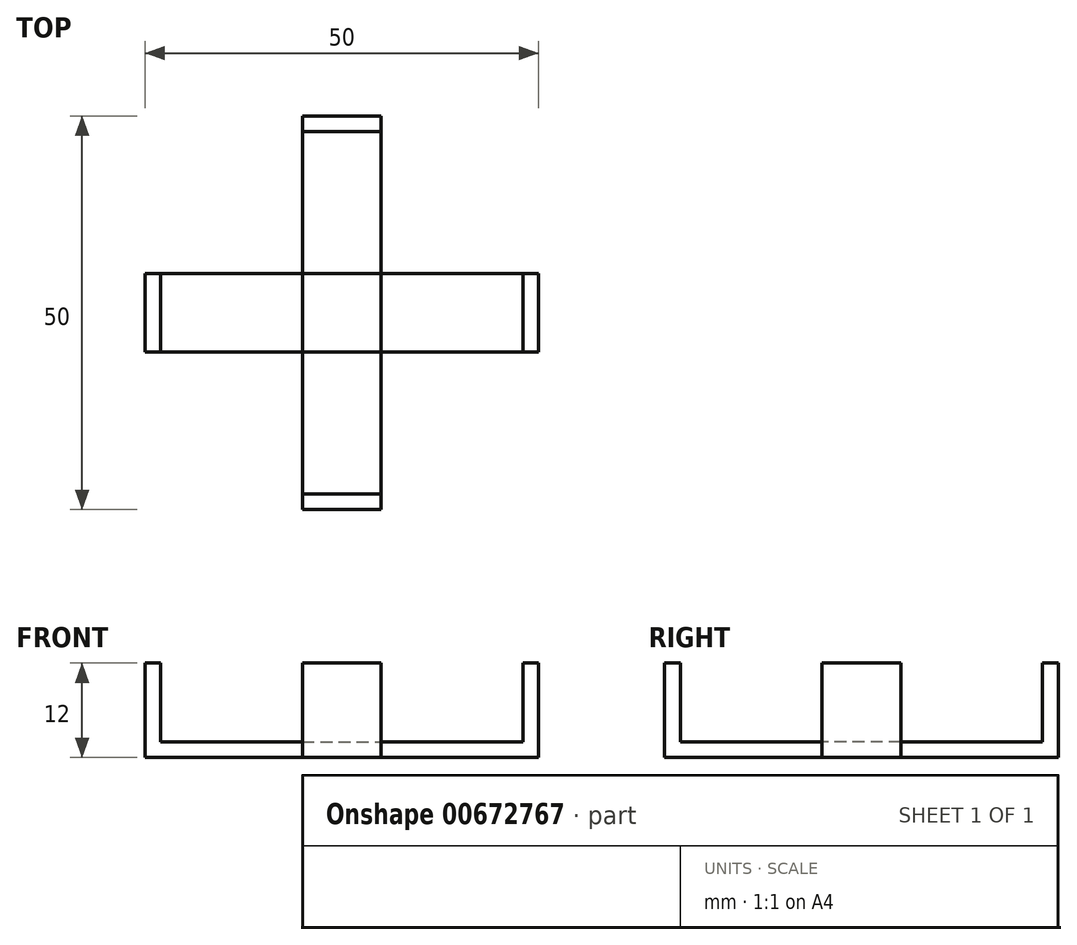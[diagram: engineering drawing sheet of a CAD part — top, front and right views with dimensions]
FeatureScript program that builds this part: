
annotation { "Feature Type Name" : "Feature", "Feature Type Description" : "" }
export const myFeature = defineFeature(function(context is Context, id is Id, definition is map)
    precondition{}
    {
        {
            var Q0;
            Q0=qCreatedBy(makeId("Top.planeOp"),FACE);
            var sketch = newSketch(context, id + "F0", { "sketchPlane" : qUnion([Q0])});
            skLineSegment(sketch, "E0.bottom", {"start": v(150, 80) * mm, "end": v(-150, 80) * mm});
            skLineSegment(sketch, "E0.top", {"start": v(150, -80) * mm, "end": v(-150, -80) * mm});
            skLineSegment(sketch, "E0.left", {"start": v(150, 80) * mm, "end": v(150, -80) * mm});
            skLineSegment(sketch, "E0.right", {"start": v(-150, 80) * mm, "end": v(-150, -80) * mm});
            skPoint(sketch, "E0.middle", {"position": v(0, 0) * mm});
            skSolve(sketch);
        }
        {
            var Q0;
            Q0=qSketchRegion(id+"F0",true);
            extrude(context, id + "F1", {"entities" : qUnion([Q0]), "depth" : 2 * mm, "offsetDistance" : 25 * mm});
        }
        {
            var Q0;
            Q0=makeQuery(id+"F1.opExtrude","CAP_FACE",FACE,{"disambiguationData":[OSD([sQuery(id+"F0.wireOp",EDGE,"E0.bottom"),sQuery(id+"F0.wireOp",EDGE,"E0.top"),sQuery(id+"F0.wireOp",EDGE,"E0.left"),sQuery(id+"F0.wireOp",EDGE,"E0.right")])],"isStart":false});
            var sketch = newSketch(context, id + "F2", { "sketchPlane" : qUnion([Q0])});
            skLineSegment(sketch, "E1.bottom", {"start": v(5, 5) * mm, "end": v(-5, 5) * mm, "construction": true});
            skLineSegment(sketch, "E1.top", {"start": v(5, -5) * mm, "end": v(-5, -5) * mm, "construction": true});
            skLineSegment(sketch, "E1.left", {"start": v(5, 5) * mm, "end": v(5, -5) * mm, "construction": true});
            skLineSegment(sketch, "E1.right", {"start": v(-5, 5) * mm, "end": v(-5, -5) * mm, "construction": true});
            skPoint(sketch, "E1.middle", {"position": v(0, 0) * mm});
            skLineSegment(sketch, "E2.bottom", {"start": v(-5, 5) * mm, "end": v(5, 5) * mm, "construction": true});
            skLineSegment(sketch, "E2.top", {"start": v(-5, 5) * mm, "end": v(5, 5) * mm, "construction": true});
            skLineSegment(sketch, "E2.left", {"start": v(-5, 5) * mm, "end": v(-5, 5) * mm});
            skLineSegment(sketch, "E2.right", {"start": v(5, 5) * mm, "end": v(5, 5) * mm});
            skLineSegment(sketch, "E3.bottom", {"start": v(-5, 5) * mm, "end": v(5, 5) * mm});
            skLineSegment(sketch, "E3.top", {"start": v(-5, 25) * mm, "end": v(5, 25) * mm});
            skLineSegment(sketch, "E3.left", {"start": v(-5, 5) * mm, "end": v(-5, 25) * mm});
            skLineSegment(sketch, "E3.right", {"start": v(5, 5) * mm, "end": v(5, 25) * mm});
            skLineSegment(sketch, "E4.bottom", {"start": v(5, 5) * mm, "end": v(25, 5) * mm});
            skLineSegment(sketch, "E4.top", {"start": v(5, -5) * mm, "end": v(25, -5) * mm});
            skLineSegment(sketch, "E4.left", {"start": v(5, 5) * mm, "end": v(5, -5) * mm});
            skLineSegment(sketch, "E4.right", {"start": v(25, 5) * mm, "end": v(25, -5) * mm});
            skLineSegment(sketch, "E5.bottom", {"start": v(5, -5) * mm, "end": v(-5, -5) * mm});
            skLineSegment(sketch, "E5.top", {"start": v(5, -25) * mm, "end": v(-5, -25) * mm});
            skLineSegment(sketch, "E5.left", {"start": v(5, -5) * mm, "end": v(5, -25) * mm});
            skLineSegment(sketch, "E5.right", {"start": v(-5, -5) * mm, "end": v(-5, -25) * mm});
            skLineSegment(sketch, "E6.bottom", {"start": v(-5, 5) * mm, "end": v(-25, 5) * mm});
            skLineSegment(sketch, "E6.top", {"start": v(-5, -5) * mm, "end": v(-25, -5) * mm});
            skLineSegment(sketch, "E6.left", {"start": v(-5, 5) * mm, "end": v(-5, -5) * mm});
            skLineSegment(sketch, "E6.right", {"start": v(-25, 5) * mm, "end": v(-25, -5) * mm});
            skSolve(sketch);
        }
        {
            var Q0;
            Q0=makeQuery(id+"F2.imprint","IMPRINT",FACE,{"disambiguationData":[TD([[makeQuery(id+"F2.imprint","IMPRINT",EDGE,{"derivedFrom":sQuery(id+"F2.wireOp",EDGE,"E3.bottom")}),1.0]])]});
            var Q1;
            Q1=makeQuery(id+"F2.imprint","IMPRINT",FACE,{"disambiguationData":[TD([[makeQuery(id+"F2.imprint","IMPRINT",EDGE,{"derivedFrom":sQuery(id+"F2.wireOp",EDGE,"E6.bottom")}),1.0]])]});
            var Q2;
            Q2=makeQuery(id+"F2.imprint","IMPRINT",FACE,{"disambiguationData":[TD([[makeQuery(id+"F2.imprint","IMPRINT",EDGE,{"derivedFrom":sQuery(id+"F2.wireOp",EDGE,"E5.bottom")}),1.0]])]});
            var Q3;
            Q3=makeQuery(id+"F2.imprint","IMPRINT",FACE,{"disambiguationData":[TD([[makeQuery(id+"F2.imprint","IMPRINT",EDGE,{"derivedFrom":sQuery(id+"F2.wireOp",EDGE,"E4.bottom")}),-1.0]])]});
            extrude(context, id + "F3", {"entities" : qUnion([Q0, Q1, Q2, Q3]), "depth" : 2 * mm, "offsetDistance" : 25 * mm});
        }
        {
            var Q0;
            Q0=makeQuery(id+"F3.opExtrude","CAP_FACE",FACE,{"disambiguationData":[OSD([sQuery(id+"F2.wireOp",EDGE,"E3.bottom"),sQuery(id+"F2.wireOp",EDGE,"E3.top"),sQuery(id+"F2.wireOp",EDGE,"E3.left"),sQuery(id+"F2.wireOp",EDGE,"E3.right")])],"isStart":false});
            var sketch = newSketch(context, id + "F4", { "sketchPlane" : qUnion([Q0])});
            skLineSegment(sketch, "E7.bottom", {"start": v(-5, 25) * mm, "end": v(5, 25) * mm});
            skLineSegment(sketch, "E7.top", {"start": v(-5, 23) * mm, "end": v(5, 23) * mm});
            skLineSegment(sketch, "E7.left", {"start": v(-5, 25) * mm, "end": v(-5, 23) * mm});
            skLineSegment(sketch, "E7.right", {"start": v(5, 25) * mm, "end": v(5, 23) * mm});
            skSolve(sketch);
        }
        {
            var Q0;
            Q0=qSketchRegion(id+"F4",true);
            extrude(context, id + "F5", {"entities" : qUnion([Q0]), "operationType" : NewBodyOperationType.ADD, "depth" : 10 * mm, "offsetDistance" : 25 * mm});
        }
        {
            var Q0;
            Q0=makeQuery(id+"F3.opExtrude","CAP_FACE",FACE,{"disambiguationData":[OSD([sQuery(id+"F2.wireOp",EDGE,"E6.bottom"),sQuery(id+"F2.wireOp",EDGE,"E6.top"),sQuery(id+"F2.wireOp",EDGE,"E6.left"),sQuery(id+"F2.wireOp",EDGE,"E6.right")])],"isStart":false});
            var sketch = newSketch(context, id + "F6", { "sketchPlane" : qUnion([Q0])});
            skLineSegment(sketch, "E8.bottom", {"start": v(-25, 5) * mm, "end": v(-23, 5) * mm});
            skLineSegment(sketch, "E8.top", {"start": v(-25, -5) * mm, "end": v(-23, -5) * mm});
            skLineSegment(sketch, "E8.left", {"start": v(-25, 5) * mm, "end": v(-25, -5) * mm});
            skLineSegment(sketch, "E8.right", {"start": v(-23, 5) * mm, "end": v(-23, -5) * mm});
            skSolve(sketch);
        }
        {
            var Q0;
            Q0=qSketchRegion(id+"F6",true);
            extrude(context, id + "F7", {"entities" : qUnion([Q0]), "operationType" : NewBodyOperationType.ADD, "depth" : 10 * mm, "offsetDistance" : 25 * mm});
        }
        {
            var Q0;
            Q0=makeQuery(id+"F3.opExtrude","CAP_FACE",FACE,{"disambiguationData":[OSD([sQuery(id+"F2.wireOp",EDGE,"E4.bottom"),sQuery(id+"F2.wireOp",EDGE,"E4.top"),sQuery(id+"F2.wireOp",EDGE,"E4.left"),sQuery(id+"F2.wireOp",EDGE,"E4.right")])],"isStart":false});
            var sketch = newSketch(context, id + "F8", { "sketchPlane" : qUnion([Q0])});
            skLineSegment(sketch, "E9.bottom", {"start": v(25, 5) * mm, "end": v(23, 5) * mm});
            skLineSegment(sketch, "E9.top", {"start": v(25, -5) * mm, "end": v(23, -5) * mm});
            skLineSegment(sketch, "E9.left", {"start": v(25, 5) * mm, "end": v(25, -5) * mm});
            skLineSegment(sketch, "E9.right", {"start": v(23, 5) * mm, "end": v(23, -5) * mm});
            skSolve(sketch);
        }
        {
            var Q0;
            Q0=qSketchRegion(id+"F8",true);
            extrude(context, id + "F9", {"entities" : qUnion([Q0]), "operationType" : NewBodyOperationType.ADD, "depth" : 10 * mm, "offsetDistance" : 25 * mm});
        }
        {
            var Q0;
            Q0=makeQuery(id+"F3.opExtrude","CAP_FACE",FACE,{"disambiguationData":[OSD([sQuery(id+"F2.wireOp",EDGE,"E5.bottom"),sQuery(id+"F2.wireOp",EDGE,"E5.top"),sQuery(id+"F2.wireOp",EDGE,"E5.left"),sQuery(id+"F2.wireOp",EDGE,"E5.right")])],"isStart":false});
            var sketch = newSketch(context, id + "F10", { "sketchPlane" : qUnion([Q0])});
            skLineSegment(sketch, "E10.bottom", {"start": v(-5, -25) * mm, "end": v(5, -25) * mm});
            skLineSegment(sketch, "E10.top", {"start": v(-5, -23) * mm, "end": v(5, -23) * mm});
            skLineSegment(sketch, "E10.left", {"start": v(-5, -25) * mm, "end": v(-5, -23) * mm});
            skLineSegment(sketch, "E10.right", {"start": v(5, -25) * mm, "end": v(5, -23) * mm});
            skSolve(sketch);
        }
        {
            var Q0;
            Q0=qSketchRegion(id+"F10",true);
            extrude(context, id + "F11", {"entities" : qUnion([Q0]), "operationType" : NewBodyOperationType.ADD, "depth" : 10 * mm, "offsetDistance" : 25 * mm});
        }
        {
            var Q0;
            Q0=makeQuery(id+"F1.opExtrude","SWEPT_BODY",BODY,{"disambiguationData":[OSD([sQuery(id+"F0.wireOp",EDGE,"E0.bottom"),sQuery(id+"F0.wireOp",EDGE,"E0.top"),sQuery(id+"F0.wireOp",EDGE,"E0.left"),sQuery(id+"F0.wireOp",EDGE,"E0.right")])]});
            deleteBodies(context, id + "F12", {"entities" : qUnion([Q0])});
        }
    });
